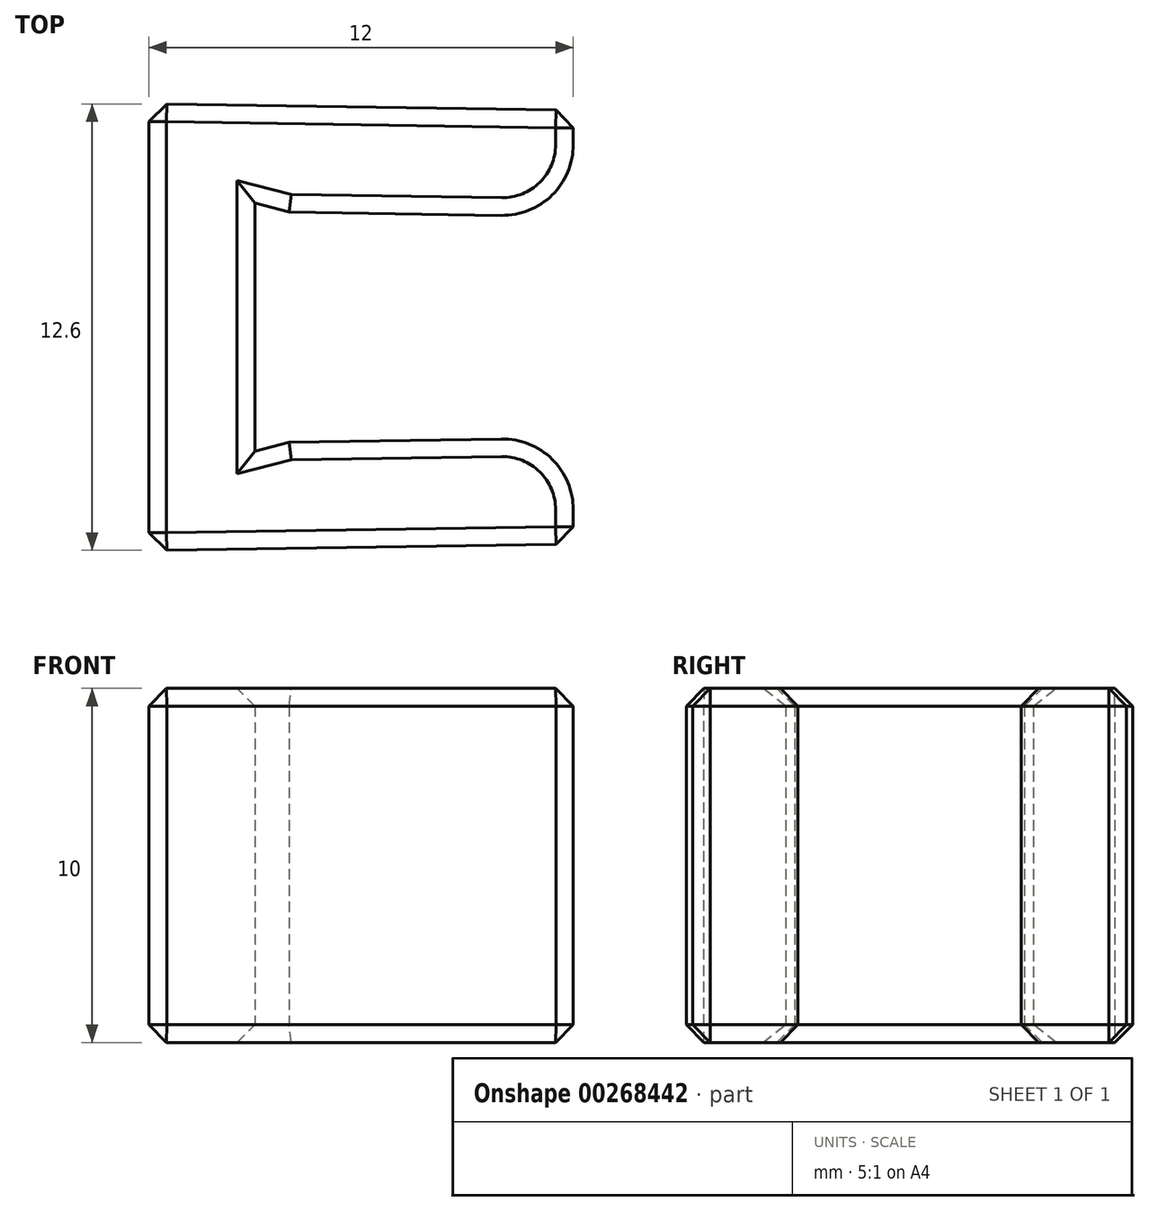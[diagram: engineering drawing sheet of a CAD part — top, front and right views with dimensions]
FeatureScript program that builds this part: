
annotation { "Feature Type Name" : "Feature", "Feature Type Description" : "" }
export const myFeature = defineFeature(function(context is Context, id is Id, definition is map)
    precondition{}
    {
        {
            var Q0;
            Q0=qCreatedBy(makeId("Top.planeOp"),FACE);
            var sketch = newSketch(context, id + "F0", { "sketchPlane" : qUnion([Q0])});
            skPoint(sketch, "E0.middle", {"position": v(0, 0) * mm});
            skLineSegment(sketch, "E1", {"start": v(-3, 6.31) * mm, "end": v(-3, -6.31) * mm});
            skLineSegment(sketch, "E2", {"start": v(-3, 0) * mm, "end": v(9, 0) * mm, "construction": true});
            skPoint(sketch, "E3", {"position": v(-3, 0) * mm});
            skLineSegment(sketch, "E4", {"start": v(-3, 6.31) * mm, "end": v(9, 6.12) * mm});
            skLineSegment(sketch, "E5", {"start": v(9, 6.12) * mm, "end": v(9, 3.12) * mm});
            skLineSegment(sketch, "E6", {"start": v(9, 3.12) * mm, "end": v(0.97, 3.25) * mm});
            skLineSegment(sketch, "E7", {"start": v(0.97, 3.25) * mm, "end": v(0, 3.5) * mm});
            skLineSegment(sketch, "E8", {"start": v(0, 3.5) * mm, "end": v(0, -3.5) * mm});
            skLineSegment(sketch, "E9", {"start": v(0, -3.5) * mm, "end": v(0.97, -3.25) * mm});
            skLineSegment(sketch, "E10", {"start": v(0.97, -3.25) * mm, "end": v(9, -3.13) * mm});
            skLineSegment(sketch, "E11", {"start": v(9, -3.13) * mm, "end": v(9, -6.12) * mm});
            skLineSegment(sketch, "E12", {"start": v(9, -6.12) * mm, "end": v(-3, -6.31) * mm});
            skLineSegment(sketch, "E13", {"start": v(9, 3.12) * mm, "end": v(9, -3.13) * mm, "construction": true});
            skPoint(sketch, "E14", {"position": v(9, 0) * mm});
            skSolve(sketch);
        }
        {
            var Q0;
            Q0=makeQuery(id+"F0.imprint","IMPRINT",FACE,{"disambiguationData":[TD([[makeQuery(id+"F0.imprint","IMPRINT",EDGE,{"derivedFrom":sQuery(id+"F0.wireOp",EDGE,"E1")}),1.0]])]});
            extrude(context, id + "F1", {"entities" : qUnion([Q0]), "depth" : 10 * mm});
        }
        {
            var Q0;
            Q0=makeQuery(id+"F1.opExtrude","SWEPT_EDGE",EDGE,{"disambiguationData":[OSD([sQuery(id+"F0.wireOp",EDGE,"E5"),sQuery(id+"F0.wireOp",EDGE,"E6")])]});
            var Q1;
            Q1=makeQuery(id+"F1.opExtrude","SWEPT_EDGE",EDGE,{"disambiguationData":[OSD([sQuery(id+"F0.wireOp",EDGE,"E10"),sQuery(id+"F0.wireOp",EDGE,"E11")])]});
            fillet(context, id + "F2", {"entities" : qUnion([Q0, Q1]), "radius" : 2 * mm, "tangentPropagation" : true, "allowEdgeOverflow" : false});
        }
        {
            var Q0;
            Q0=makeQuery(id+"F1.opExtrude","SWEPT_FACE",FACE,{"disambiguationData":[OSD([sQuery(id+"F0.wireOp",EDGE,"E4")])]});
            var Q1;
            Q1=makeQuery(id+"F1.opExtrude","SWEPT_FACE",FACE,{"disambiguationData":[OSD([sQuery(id+"F0.wireOp",EDGE,"E1")])]});
            var Q2;
            Q2=makeQuery(id+"F1.opExtrude","SWEPT_FACE",FACE,{"disambiguationData":[OSD([sQuery(id+"F0.wireOp",EDGE,"E12")])]});
            var Q3;
            Q3=makeQuery(id+"F1.opExtrude","CAP_FACE",FACE,{"disambiguationData":[OSD([sQuery(id+"F0.wireOp",EDGE,"E1"),sQuery(id+"F0.wireOp",EDGE,"E4"),sQuery(id+"F0.wireOp",EDGE,"E5"),sQuery(id+"F0.wireOp",EDGE,"E6"),sQuery(id+"F0.wireOp",EDGE,"E7"),sQuery(id+"F0.wireOp",EDGE,"E8"),sQuery(id+"F0.wireOp",EDGE,"E9"),sQuery(id+"F0.wireOp",EDGE,"E10"),sQuery(id+"F0.wireOp",EDGE,"E11"),sQuery(id+"F0.wireOp",EDGE,"E12")])],"isStart":false});
            var Q4;
            Q4=makeQuery(id+"F1.opExtrude","CAP_FACE",FACE,{"disambiguationData":[OSD([sQuery(id+"F0.wireOp",EDGE,"E1"),sQuery(id+"F0.wireOp",EDGE,"E4"),sQuery(id+"F0.wireOp",EDGE,"E5"),sQuery(id+"F0.wireOp",EDGE,"E6"),sQuery(id+"F0.wireOp",EDGE,"E7"),sQuery(id+"F0.wireOp",EDGE,"E8"),sQuery(id+"F0.wireOp",EDGE,"E9"),sQuery(id+"F0.wireOp",EDGE,"E10"),sQuery(id+"F0.wireOp",EDGE,"E11"),sQuery(id+"F0.wireOp",EDGE,"E12")])],"isStart":true});
            chamfer(context, id + "F3", {"entities" : qUnion([Q0, Q1, Q2, Q3, Q4]), "width" : .5 * mm, "tangentPropagation" : true});
        }
    });
